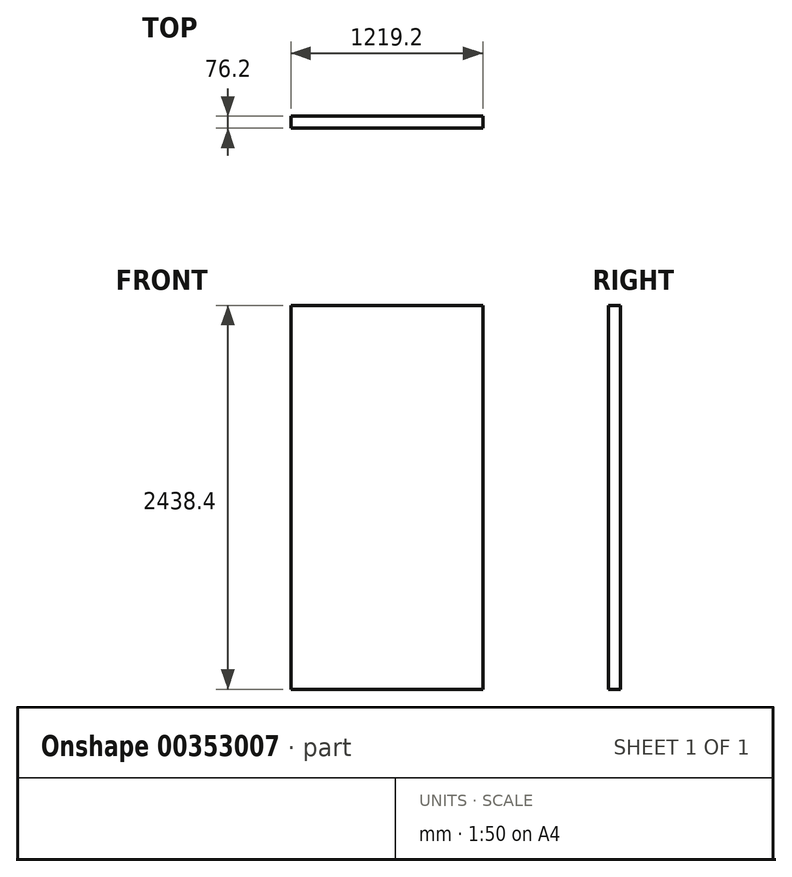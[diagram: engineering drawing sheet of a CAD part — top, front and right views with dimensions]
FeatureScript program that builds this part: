
annotation { "Feature Type Name" : "Feature", "Feature Type Description" : "" }
export const myFeature = defineFeature(function(context is Context, id is Id, definition is map)
    precondition{}
    {
        {
            var Q0;
            Q0=qCreatedBy(makeId("Front.planeOp"),FACE);
            var sketch = newSketch(context, id + "F0", { "sketchPlane" : qUnion([Q0])});
            skLineSegment(sketch, "E0.bottom", {"start": v(-623.38, 1482.9) * mm, "end": v(595.82, 1482.9) * mm});
            skLineSegment(sketch, "E0.top", {"start": v(-623.38, -955.5) * mm, "end": v(595.82, -955.5) * mm});
            skLineSegment(sketch, "E0.left", {"start": v(-623.38, 1482.9) * mm, "end": v(-623.38, -955.5) * mm});
            skLineSegment(sketch, "E0.right", {"start": v(595.82, 1482.9) * mm, "end": v(595.82, -955.5) * mm});
            skSolve(sketch);
        }
        {
            var Q0;
            Q0=makeQuery(id+"F0.imprint","IMPRINT",FACE,{"disambiguationData":[TD([[makeQuery(id+"F0.imprint","IMPRINT",EDGE,{"derivedFrom":sQuery(id+"F0.wireOp",EDGE,"E0.bottom")}),-1.0]])]});
            extrude(context, id + "F1", {"entities" : qUnion([Q0]), "depth" : 76.2 * mm});
        }
    });
